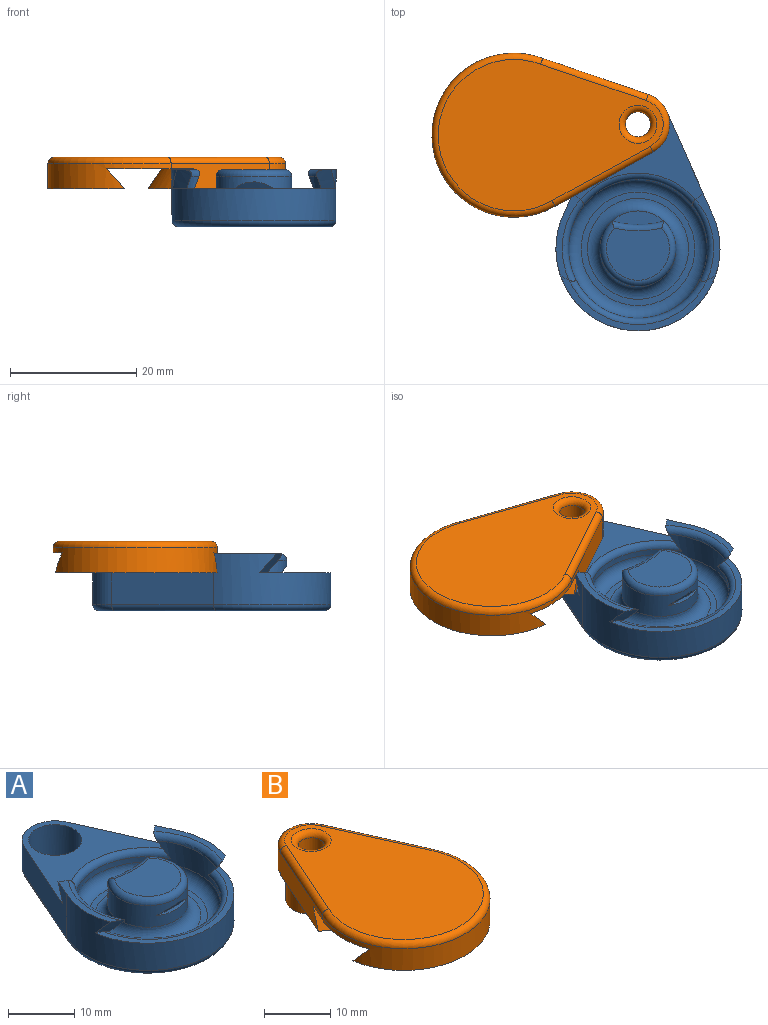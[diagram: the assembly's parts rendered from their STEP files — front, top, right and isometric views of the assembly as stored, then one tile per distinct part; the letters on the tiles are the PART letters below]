
ASSEMBLY  parts=2 mates=1
PART A: 36 faces, bbox 28.2x39.2x9 mm
  f0: cone r=26.99mm half-angle=33.7deg, axis (0,0,1), area 10mm2, adj f3,f9,f16,f17,f32,f34
  f1: cone r=26.99mm half-angle=33.7deg, axis (0,0,1), area 10mm2, adj f4,f9,f15,f17,f33,f34
  f2: cone r=15mm half-angle=33.7deg, axis (0,0,-1), area 8.4mm2, adj f4,f7,f10,f15,f33,f35
  f3: plane 13.78x3.89mm, normal (0,0,1), area 14.3mm2, adj f0,f6,f9,f12,f32
  f4: plane 13.78x3.89mm, normal (0,0,1), area 14.3mm2, adj f1,f2,f9,f10,f33
  f5: plane 10x8.28mm, normal (0,0,1), area 67.4mm2, adj f30,f31
  f6: cone r=15mm half-angle=33.7deg, axis (0,0,-1), area 8.4mm2, adj f3,f7,f12,f15,f32,f35
  f7: plane 22.32x18.54mm, normal (0,0,1), area 133.5mm2, adj f2,f6,f10,f11,f12,f13,f35
  f8: plane 9.83x3.28mm, normal (0,0,1), area 22.4mm2, adj f19,f23
  f9: cylinder r=13mm len=26mm, axis (0,0,1), area 314.2mm2, adj f0,f1,f3,f4,f10,f12,f17,f27
  f10: plane 16.29x8.04mm, normal (0.91,0.41,0), area 96.6mm2, adj f2,f4,f7,f9,f11,f29
  f11: cylinder r=5mm len=9.14mm, axis (0,0,1), area 57.7mm2, adj f7,f10,f12,f28
  f12: plane 16.19x8.04mm, normal (-0.91,0.41,0), area 95.8mm2, adj f3,f6,f7,f9,f11,f26
  f13: cylinder r=4mm len=8mm, axis (0,0,1), area 150.8mm2, adj f7,f14,f28
  f14: plane 33.34x24mm, normal (0,0,-1), area 542.8mm2, adj f13,f26,f27,f29
  f15: cylinder r=11mm len=22mm, axis (0,0,-1), area 122.9mm2, adj f1,f2,f6,f16,f25,f32,f33,f34
  f16: cylinder r=11mm len=3mm, axis (0,0,-1), area 4.1mm2, adj f0,f15,f32
  f17: plane 25.78x11.31mm, normal (0,0,1), area 35.2mm2, adj f0,f1,f9,f34
  f18: plane 18x18mm, normal (0,0,1), area 53.4mm2, adj f24,f25
  f19: cylinder r=6mm len=12mm, axis (0,0,-1), area 124.3mm2, adj f8,f20,f21,f22,f23,f24,f30,f31
  f20: cylinder r=6mm len=2mm, axis (0,0,-1), area 1.4mm2, adj f19,f23,f30,f31
  f21: plane 6.44x0.94mm, normal (0,0,1), area 3.2mm2, adj f19,f22
  f22: cone r=26.99mm half-angle=33.7deg, axis (0,0,1), area 5.8mm2, adj f19,f21
  f23: cone r=15mm half-angle=33.7deg, axis (0,0,-1), area 16.1mm2, adj f8,f19,f20,f30
  f24: torus R=8mm, axis (0,0,1), area 132.8mm2, adj f18,f19
  f25: torus R=9mm, axis (0,0,1), area 202.8mm2, adj f15,f18
  f26: cylinder r=1mm len=16.57mm, axis (0.41,0.91,0), area 27.8mm2, adj f12,f14,f27,f28
  f27: torus R=12mm, axis (0,0,1), area 79.9mm2, adj f9,f14,f26,f29
  f28: torus R=4mm, axis (0,0,1), area 16.8mm2, adj f11,f13,f26,f29
  f29: cylinder r=1mm len=16.66mm, axis (0.41,-0.91,0), area 27.9mm2, adj f10,f14,f27,f28
  f30: torus R=16.87mm, axis (0,0,1), area 17.6mm2, adj f5,f19,f20,f23,f31
  f31: torus R=5mm, axis (0,0,1), area 41.7mm2, adj f5,f19,f20,f30
  f32: torus R=12mm, axis (0,0,1), area 20.5mm2, adj f0,f3,f6,f15,f16
  f33: torus R=12mm, axis (0,0,1), area 20.5mm2, adj f1,f2,f4,f15
  f34: torus R=12mm, axis (0,0,1), area 48.5mm2, adj f0,f1,f15,f17
  f35: torus R=12mm, axis (0,0,1), area 37.7mm2, adj f2,f6,f7,f15
PART B: 19 faces, bbox 28.2x39.3x11.1 mm
  f0: cylinder r=13mm len=26mm, axis (0,0,-1), area 150.5mm2, adj f1,f3,f6,f7,f8,f15
  f1: plane 16.3x7.26mm, normal (0.91,0.41,0), area 61.8mm2, adj f0,f2,f4,f5,f8,f13
  f2: cylinder r=5mm len=9.14mm, axis (0,0,-1), area 46.1mm2, adj f1,f3,f4,f14
  f3: plane 16.2x7.21mm, normal (-0.91,0.41,0), area 61.7mm2, adj f0,f2,f4,f5,f8,f16
  f4: plane 22.11x21.76mm, normal (0,0,-1), area 265.8mm2, adj f1,f2,f3,f5,f11
  f5: cone r=14.63mm half-angle=33.7deg, axis (0,0,-1), area 89.7mm2, adj f1,f3,f4,f8
  f6: cone r=27.36mm half-angle=33.7deg, axis (0,0,1), area 100.4mm2, adj f0,f7,f8
  f7: plane 25.69x11mm, normal (0,0,-1), area 152.6mm2, adj f0,f6
  f8: plane 26x16.83mm, normal (0,0,-1), area 330.8mm2, adj f0,f1,f3,f5,f6
  f9: plane 35.72x24mm, normal (0,0,1), area 564.8mm2, adj f13,f14,f15,f16,f18
  f10: cylinder r=2mm len=9mm, axis (0,0,1), area 113.1mm2, adj f17,f18
  f11: cylinder r=3.8mm len=7.6mm, axis (0,0,1), area 143.3mm2, adj f4,f12
  f12: plane 7.6x7.6mm, normal (0,0,-1), area 17.1mm2, adj f11,f17
  f13: cylinder r=1mm len=16.66mm, axis (-0.41,0.91,0), area 27.9mm2, adj f1,f9,f14,f15
  f14: torus R=4mm, axis (0,0,1), area 16.8mm2, adj f2,f9,f13,f16
  f15: torus R=12mm, axis (0,0,1), area 79.9mm2, adj f0,f9,f13,f16
  f16: cylinder r=1mm len=16.57mm, axis (-0.41,-0.91,0), area 27.8mm2, adj f3,f9,f14,f15
  f17: torus R=3mm, axis (0,0,-1), area 23.3mm2, adj f10,f12
  f18: torus R=3mm, axis (0,0,1), area 23.3mm2, adj f9,f10
PLACE A t=(-8.62,-6.79,11.51)mm
PLACE B rot(axis=(0,0,-1),85deg) t=(-28.26,11.21,11.51)mm
MATE revolute A.f11 <-> B.f2  axis (0,0,-1) through (-8.62,12.93,9.51)mm
